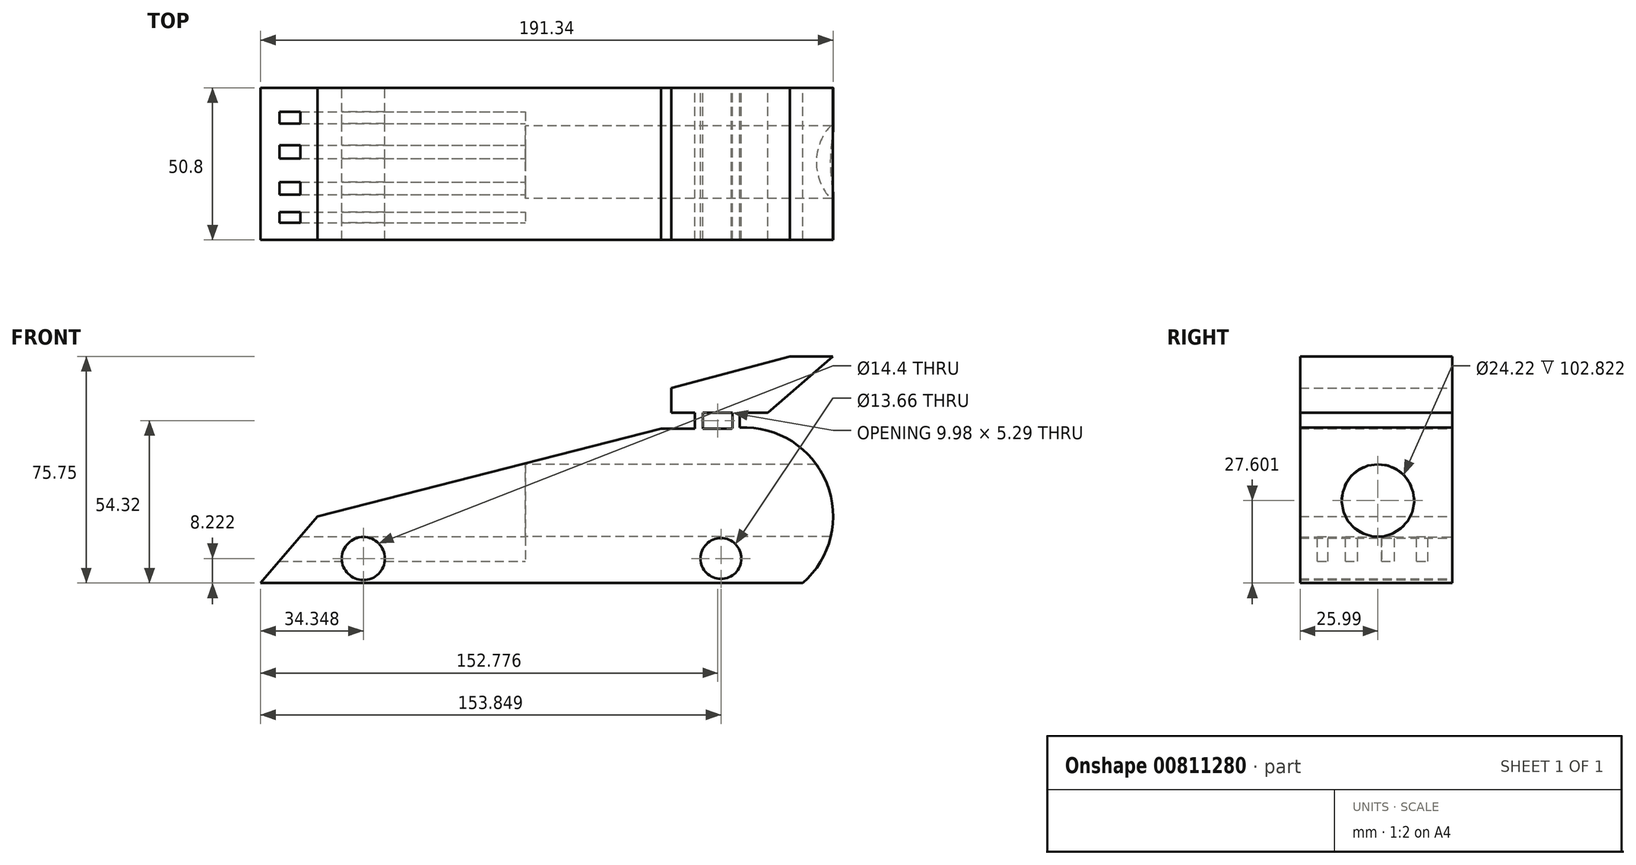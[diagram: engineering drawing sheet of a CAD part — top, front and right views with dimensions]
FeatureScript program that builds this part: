
annotation { "Feature Type Name" : "Feature", "Feature Type Description" : "" }
export const myFeature = defineFeature(function(context is Context, id is Id, definition is map)
    precondition{}
    {
        {
            var Q0;
            Q0=qCreatedBy(makeId("Front.planeOp"),FACE);
            var sketch = newSketch(context, id + "F0", { "sketchPlane" : qUnion([Q0])});
            skLineSegment(sketch, "E0.bottom", {"start": v(45.36, 38.76) * mm, "end": v(77.52, 38.76) * mm});
            skLineSegment(sketch, "E0.top", {"start": v(-88.52, -12.92) * mm, "end": v(92.64, -12.92) * mm});
            skLineSegment(sketch, "E1", {"start": v(-88.52, -12.92) * mm, "end": v(-69.44, 9.4) * mm});
            skLineSegment(sketch, "E2", {"start": v(-69.44, 9.4) * mm, "end": v(0, 27.16) * mm});
            skArc(sketch, "E3", {"start": v(92.64, -12.92) * mm, "mid": v(100.1, 21.83) * mm, "end": v(68.85, 38.76) * mm});
            skCircle(sketch, "E4", {"center": v(-54.17, -4.7) * mm, "radius": 7.2 * mm});
            skCircle(sketch, "E5", {"center": v(65.33, -4.7) * mm, "radius": 6.83 * mm});
            skLineSegment(sketch, "E6", {"start": v(45.36, 38.76) * mm, "end": v(0, 27.16) * mm});
            skSolve(sketch);
        }
        {
            var Q0;
            Q0 = qSketchRegion(id + "F0", true);
            extrude(context, id + "F1", {"entities" : qUnion([Q0]), "depth" : 50.8 * mm, "offsetDistance" : 25.4 * mm});
        }
        {
            var Q0;
            Q0=qCreatedBy(makeId("Right.planeOp"),FACE);
            var sketch = newSketch(context, id + "F2", { "sketchPlane" : qUnion([Q0])});
            skCircle(sketch, "E7", {"center": v(-24.81, 14.68) * mm, "radius": 12.1 * mm});
            skSolve(sketch);
        }
        {
            var Q0;
            Q0 = qSketchRegion(id + "F2", true);
            extrude(context, id + "F3", {"entities" : qUnion([Q0]), "operationType" : NewBodyOperationType.REMOVE, "depth" : 127 * mm, "offsetDistance" : 25.4 * mm});
        }
        {
            var Q0;
            Q0=qCreatedBy(makeId("Front.planeOp"),FACE);
            var sketch = newSketch(context, id + "F4", { "sketchPlane" : qUnion([Q0])});
            skLineSegment(sketch, "E8.bottom", {"start": v(48.7, 44.04) * mm, "end": v(81, 44.04) * mm});
            skLineSegment(sketch, "E8.left", {"start": v(48.7, 44.04) * mm, "end": v(48.7, 52.26) * mm});
            skLineSegment(sketch, "E9", {"start": v(48.7, 52.26) * mm, "end": v(88.33, 62.83) * mm});
            skLineSegment(sketch, "E10", {"start": v(88.33, 62.83) * mm, "end": v(102.72, 62.83) * mm});
            skLineSegment(sketch, "E11", {"start": v(102.72, 62.83) * mm, "end": v(81, 44.04) * mm});
            skLineSegment(sketch, "E12.bottom", {"start": v(59.26, 44.04) * mm, "end": v(56.62, 44.04) * mm});
            skLineSegment(sketch, "E12.top", {"start": v(59.26, 37.58) * mm, "end": v(56.62, 37.58) * mm});
            skLineSegment(sketch, "E12.left", {"start": v(59.26, 44.04) * mm, "end": v(59.26, 37.58) * mm});
            skLineSegment(sketch, "E12.right", {"start": v(56.62, 44.04) * mm, "end": v(56.62, 37.58) * mm});
            skLineSegment(sketch, "E13.bottom", {"start": v(69.25, 44.04) * mm, "end": v(71.6, 44.04) * mm});
            skLineSegment(sketch, "E13.top", {"start": v(69.25, 36.7) * mm, "end": v(71.6, 36.7) * mm});
            skLineSegment(sketch, "E13.left", {"start": v(69.25, 44.04) * mm, "end": v(69.25, 36.7) * mm});
            skLineSegment(sketch, "E13.right", {"start": v(71.6, 44.04) * mm, "end": v(71.6, 36.7) * mm});
            skSolve(sketch);
        }
        {
            var Q0;
            Q0 = qSketchRegion(id + "F4", true);
            extrude(context, id + "F5", {"entities" : qUnion([Q0]), "operationType" : NewBodyOperationType.ADD, "depth" : 50.8 * mm, "offsetDistance" : 25.4 * mm});
        }
        {
            var Q0;
            Q0=qCreatedBy(makeId("Right.planeOp"),FACE);
            var sketch = newSketch(context, id + "F6", { "sketchPlane" : qUnion([Q0])});
            skLineSegment(sketch, "E14.bottom", {"start": v(-8.07, 2.64) * mm, "end": v(-11.9, 2.64) * mm});
            skLineSegment(sketch, "E14.top", {"start": v(-8.07, -5.58) * mm, "end": v(-11.9, -5.58) * mm});
            skLineSegment(sketch, "E14.left", {"start": v(-8.07, 2.64) * mm, "end": v(-8.07, -5.58) * mm});
            skLineSegment(sketch, "E14.right", {"start": v(-11.9, 2.64) * mm, "end": v(-11.9, -5.58) * mm});
            skLineSegment(sketch, "E15.bottom", {"start": v(-19.23, 2.64) * mm, "end": v(-23.64, 2.64) * mm});
            skLineSegment(sketch, "E15.top", {"start": v(-19.23, -5.58) * mm, "end": v(-23.64, -5.58) * mm});
            skLineSegment(sketch, "E15.left", {"start": v(-19.23, 2.64) * mm, "end": v(-19.23, -5.58) * mm});
            skLineSegment(sketch, "E15.right", {"start": v(-23.64, 2.64) * mm, "end": v(-23.64, -5.58) * mm});
            skLineSegment(sketch, "E16.bottom", {"start": v(-31.56, 2.64) * mm, "end": v(-35.67, 2.64) * mm});
            skLineSegment(sketch, "E16.top", {"start": v(-31.56, -5.58) * mm, "end": v(-35.67, -5.58) * mm});
            skLineSegment(sketch, "E16.left", {"start": v(-31.56, 2.64) * mm, "end": v(-31.56, -5.58) * mm});
            skLineSegment(sketch, "E16.right", {"start": v(-35.67, 2.64) * mm, "end": v(-35.67, -5.58) * mm});
            skLineSegment(sketch, "E17.bottom", {"start": v(-41.55, 2.64) * mm, "end": v(-45.07, 2.64) * mm});
            skLineSegment(sketch, "E17.top", {"start": v(-41.55, -5.58) * mm, "end": v(-45.07, -5.58) * mm});
            skLineSegment(sketch, "E17.left", {"start": v(-41.55, 2.64) * mm, "end": v(-41.55, -5.58) * mm});
            skLineSegment(sketch, "E17.right", {"start": v(-45.07, 2.64) * mm, "end": v(-45.07, -5.58) * mm});
            skSolve(sketch);
        }
        {
            var Q0;
            Q0 = qSketchRegion(id + "F6", true);
            extrude(context, id + "F7", {"entities" : qUnion([Q0]), "operationType" : NewBodyOperationType.REMOVE, "oppositeDirection" : true, "depth" : 101.6 * mm, "offsetDistance" : 25.4 * mm});
        }
    });
